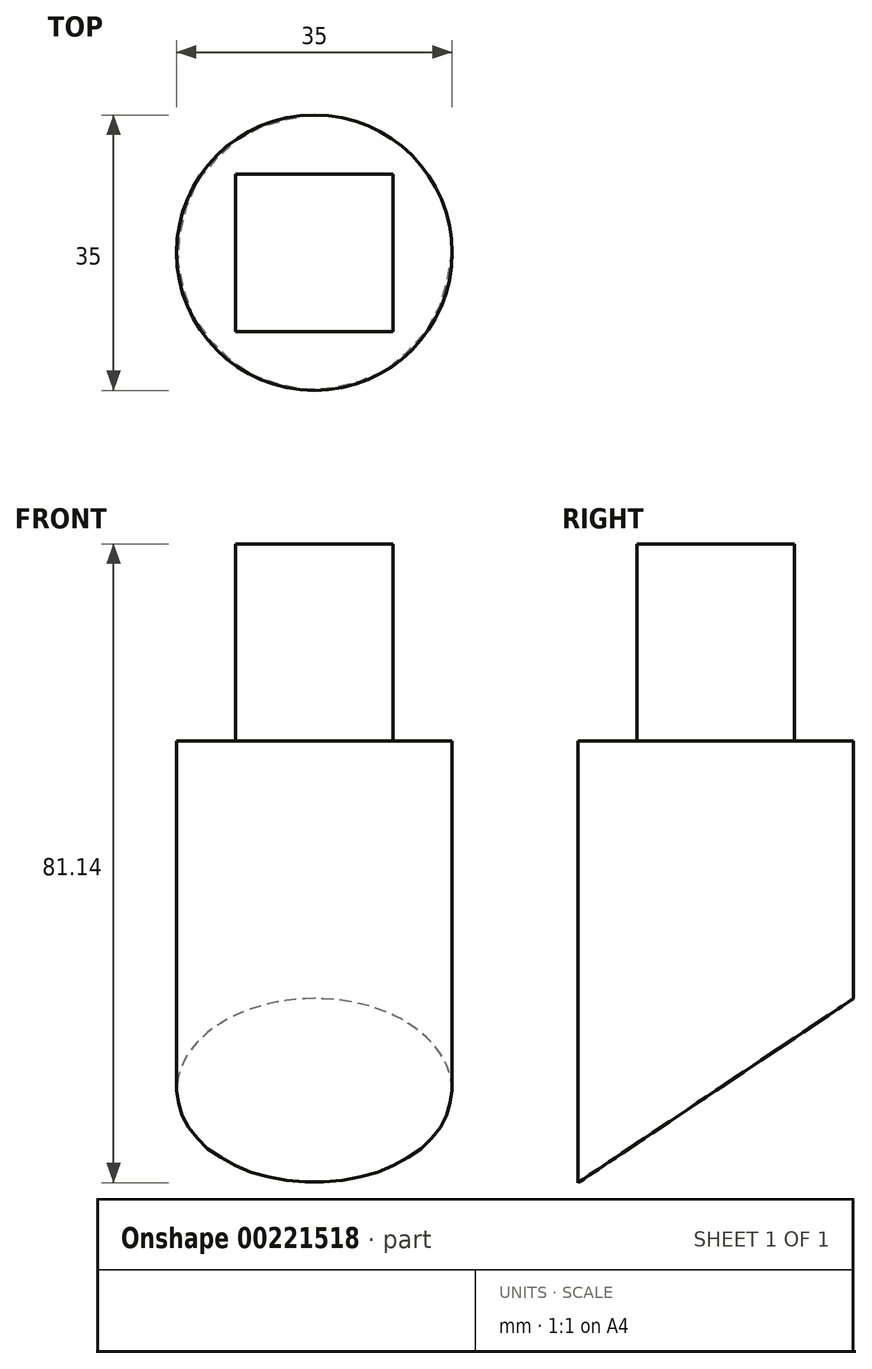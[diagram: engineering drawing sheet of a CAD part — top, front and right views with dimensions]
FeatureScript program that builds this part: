
annotation { "Feature Type Name" : "Feature", "Feature Type Description" : "" }
export const myFeature = defineFeature(function(context is Context, id is Id, definition is map)
    precondition{}
    {
        {
            var Q0;
            Q0=qCreatedBy(makeId("Top.planeOp"),FACE);
            var sketch = newSketch(context, id + "F0", { "sketchPlane" : qUnion([Q0])});
            skCircle(sketch, "E0", {"center": v(0, 0) * mm, "radius": 17.5 * mm});
            skSolve(sketch);
        }
        {
            var Q0;
            Q0=makeQuery(id+"F0.imprint","IMPRINT",FACE,{"disambiguationData":[TD([[makeQuery(id+"F0.imprint","IMPRINT",EDGE,{"derivedFrom":sQuery(id+"F0.wireOp",EDGE,"E0")}),1.0]])]});
            extrude(context, id + "F1", {"entities" : qUnion([Q0]), "endBound" : BoundingType.SYMMETRIC, "oppositeDirection" : true, "depth" : 100 * mm});
        }
        {
            var Q0;
            Q0=makeQuery(id+"F1.opExtrude","CAP_FACE",FACE,{"disambiguationData":[OSD([sQuery(id+"F0.wireOp",EDGE,"E0")])],"isStart":true});
            var sketch = newSketch(context, id + "F2", { "sketchPlane" : qUnion([Q0])});
            skLineSegment(sketch, "E1.bottom", {"start": v(10, -10) * mm, "end": v(-10, -10) * mm});
            skLineSegment(sketch, "E1.top", {"start": v(10, 10) * mm, "end": v(-10, 10) * mm});
            skLineSegment(sketch, "E1.left", {"start": v(10, -10) * mm, "end": v(10, 10) * mm});
            skLineSegment(sketch, "E1.right", {"start": v(-10, -10) * mm, "end": v(-10, 10) * mm});
            skPoint(sketch, "E1.middle", {"position": v(0, 0) * mm});
            skSolve(sketch);
        }
        {
            var Q0;
            Q0 = qSketchRegion(id + "F2", true);
            extrude(context, id + "F3", {"entities" : qUnion([Q0]), "operationType" : NewBodyOperationType.ADD, "depth" : 25 * mm});
        }
        {
            var Q0;
            Q0=qCreatedBy(makeId("Right.planeOp"),FACE);
            var sketch = newSketch(context, id + "F4", { "sketchPlane" : qUnion([Q0])});
            skLineSegment(sketch, "E2", {"start": v(28.84, 24.85) * mm, "end": v(-43.48, -23.51) * mm});
            skLineSegment(sketch, "E3", {"start": v(-43.48, -23.51) * mm, "end": v(-43.48, -61) * mm});
            skLineSegment(sketch, "E4", {"start": v(-43.48, -61) * mm, "end": v(41.7, -61) * mm});
            skLineSegment(sketch, "E5", {"start": v(41.7, -61) * mm, "end": v(28.84, 24.85) * mm});
            skSolve(sketch);
        }
        {
            var Q0;
            Q0=makeQuery(id+"F4.imprint","IMPRINT",FACE,{"disambiguationData":[TD([[makeQuery(id+"F4.imprint","IMPRINT",EDGE,{"derivedFrom":sQuery(id+"F4.wireOp",EDGE,"E2")}),1.0]])]});
            extrude(context, id + "F5", {"entities" : qUnion([Q0]), "operationType" : NewBodyOperationType.REMOVE, "endBound" : BoundingType.SYMMETRIC, "oppositeDirection" : true, "depth" : 50 * mm});
        }
    });
